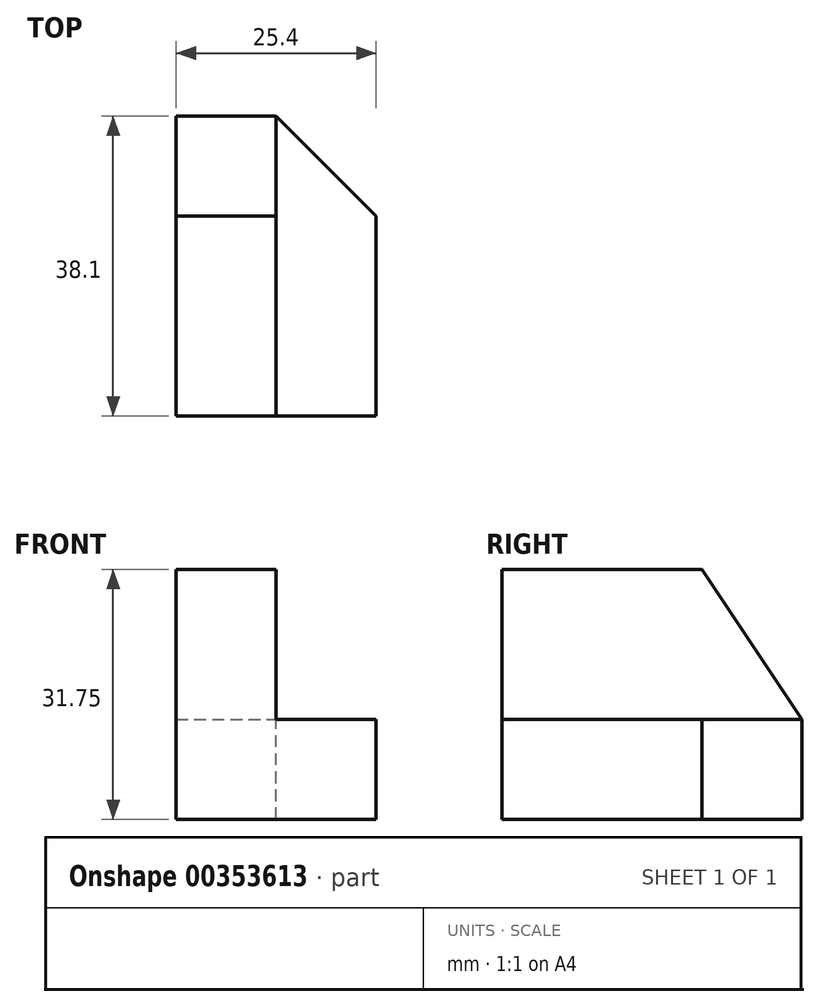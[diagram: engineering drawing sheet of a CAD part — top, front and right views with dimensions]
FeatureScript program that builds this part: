
annotation { "Feature Type Name" : "Feature", "Feature Type Description" : "" }
export const myFeature = defineFeature(function(context is Context, id is Id, definition is map)
    precondition{}
    {
        {
            var Q0;
            Q0=qCreatedBy(makeId("Front.planeOp"),FACE);
            var sketch = newSketch(context, id + "F0", { "sketchPlane" : qUnion([Q0])});
            skLineSegment(sketch, "E0", {"start": v(0, 0) * mm, "end": v(0, 31.75) * mm});
            skLineSegment(sketch, "E1", {"start": v(0, 31.75) * mm, "end": v(12.7, 31.75) * mm});
            skLineSegment(sketch, "E2", {"start": v(12.7, 31.75) * mm, "end": v(12.7, 12.7) * mm});
            skLineSegment(sketch, "E3", {"start": v(12.7, 12.7) * mm, "end": v(25.4, 12.7) * mm});
            skLineSegment(sketch, "E4", {"start": v(25.4, 12.7) * mm, "end": v(25.4, 0) * mm});
            skLineSegment(sketch, "E5", {"start": v(25.4, 0) * mm, "end": v(0, 0) * mm});
            skSolve(sketch);
        }
        {
            var Q0;
            Q0=makeQuery(id+"F0.imprint","IMPRINT",FACE,{"disambiguationData":[TD([[makeQuery(id+"F0.imprint","IMPRINT",EDGE,{"derivedFrom":sQuery(id+"F0.wireOp",EDGE,"E0")}),-1.0]])]});
            extrude(context, id + "F1", {"entities" : qUnion([Q0]), "depth" : 38.1 * mm});
        }
        {
            var Q0;
            Q0=makeQuery(id+"F1.opExtrude","SWEPT_FACE",FACE,{"disambiguationData":[OSD([sQuery(id+"F0.wireOp",EDGE,"E3")])]});
            var sketch = newSketch(context, id + "F2", { "sketchPlane" : qUnion([Q0])});
            skLineSegment(sketch, "E6", {"start": v(12.7, 0) * mm, "end": v(25.4, -12.7) * mm});
            skLineSegment(sketch, "E7", {"start": v(12.7, 0) * mm, "end": v(25.4, 0) * mm});
            skLineSegment(sketch, "E8", {"start": v(25.4, 0) * mm, "end": v(25.4, -12.7) * mm});
            skSolve(sketch);
        }
        {
            var Q0;
            Q0=makeQuery(id+"F2.imprint","IMPRINT",FACE,{"disambiguationData":[TD([[makeQuery(id+"F2.imprint","IMPRINT",EDGE,{"derivedFrom":sQuery(id+"F2.wireOp",EDGE,"E6")}),1.0]])]});
            extrude(context, id + "F3", {"entities" : qUnion([Q0]), "operationType" : NewBodyOperationType.REMOVE, "oppositeDirection" : true, "depth" : 25.4 * mm});
        }
        {
            var Q0;
            Q0=makeQuery(id+"F1.opExtrude","SWEPT_FACE",FACE,{"disambiguationData":[OSD([sQuery(id+"F0.wireOp",EDGE,"E2")])]});
            var sketch = newSketch(context, id + "F4", { "sketchPlane" : qUnion([Q0])});
            skLineSegment(sketch, "E9", {"start": v(0, 12.7) * mm, "end": v(-12.7, 31.75) * mm});
            skLineSegment(sketch, "E10", {"start": v(-12.7, 31.75) * mm, "end": v(0, 31.75) * mm});
            skLineSegment(sketch, "E11", {"start": v(0, 31.75) * mm, "end": v(0, 12.7) * mm});
            skSolve(sketch);
        }
        {
            var Q0;
            Q0=makeQuery(id+"F4.imprint","IMPRINT",FACE,{"disambiguationData":[TD([[makeQuery(id+"F4.imprint","IMPRINT",EDGE,{"derivedFrom":sQuery(id+"F4.wireOp",EDGE,"E9")}),-1.0]])]});
            extrude(context, id + "F5", {"entities" : qUnion([Q0]), "operationType" : NewBodyOperationType.REMOVE, "oppositeDirection" : true, "depth" : 38.1 * mm});
        }
    });
